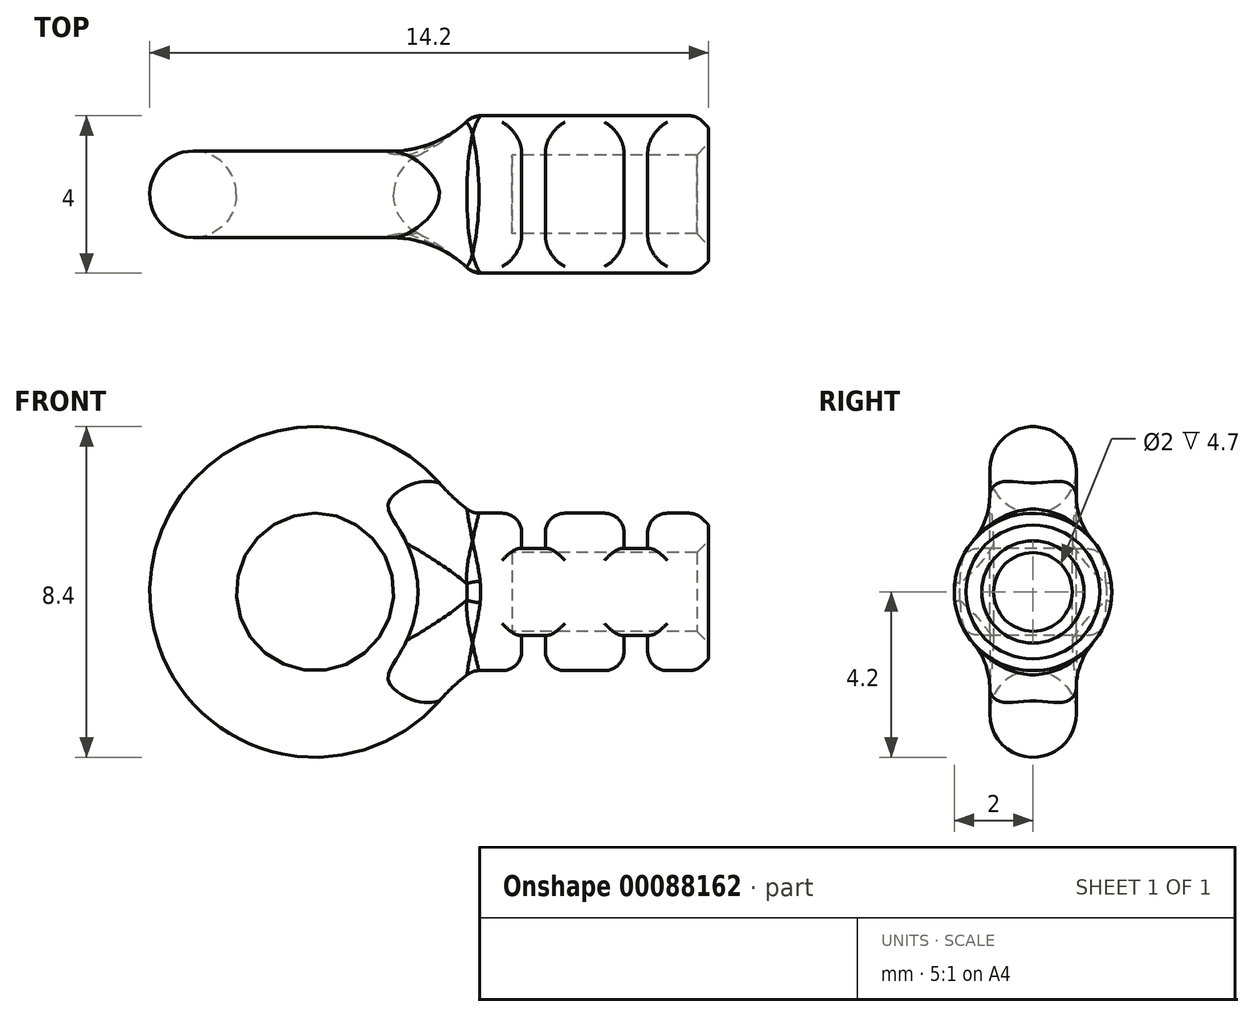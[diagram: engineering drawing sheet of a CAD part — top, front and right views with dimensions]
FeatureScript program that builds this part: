
annotation { "Feature Type Name" : "Feature", "Feature Type Description" : "" }
export const myFeature = defineFeature(function(context is Context, id is Id, definition is map)
    precondition{}
    {
        {
            var Q0;
            Q0=qCreatedBy(makeId("Top.planeOp"),FACE);
            var sketch = newSketch(context, id + "F0", { "sketchPlane" : qUnion([Q0])});
            skLineSegment(sketch, "E0", {"start": v(-5, 0) * mm, "end": v(-5, 1) * mm});
            skLineSegment(sketch, "E1", {"start": v(-5, 1) * mm, "end": v(0, 1) * mm});
            skLineSegment(sketch, "E2", {"start": v(0, 1) * mm, "end": v(0, 2) * mm});
            skLineSegment(sketch, "E3", {"start": v(0, 2) * mm, "end": v(-6, 2) * mm});
            skLineSegment(sketch, "E4", {"start": v(-6, 2) * mm, "end": v(-8, 0) * mm});
            skLineSegment(sketch, "E5", {"start": v(-8, 0) * mm, "end": v(-5, 0) * mm});
            skSolve(sketch);
        }
        {
            var Q0;
            Q0=makeQuery(id+"F0.imprint","IMPRINT",FACE,{"disambiguationData":[TD([[makeQuery(id+"F0.imprint","IMPRINT",EDGE,{"derivedFrom":sQuery(id+"F0.wireOp",EDGE,"E0")}),1.0]])]});
            var Q1;
            Q1=sQuery(id+"F0.wireOp",EDGE,"E5");
            revolve(context, id + "F1", {"entities" : qUnion([Q0]), "axis" : qUnion([Q1]), "revolveType" : RevolveType.FULL});
        }
        {
            var Q0;
            Q0=makeQuery(id+"F1.opRevolve","SWEPT_EDGE",EDGE,{"disambiguationData":[OSD([sQuery(id+"F0.wireOp",EDGE,"E1"),sQuery(id+"F0.wireOp",EDGE,"E2")])]});
            var Q1;
            Q1=makeQuery(id+"F1.opRevolve","SWEPT_EDGE",EDGE,{"disambiguationData":[OSD([sQuery(id+"F0.wireOp",EDGE,"E2"),sQuery(id+"F0.wireOp",EDGE,"E3")])]});
            chamfer(context, id + "F2", {"entities" : qUnion([Q0, Q1]), "width" : .3 * mm, "tangentPropagation" : true});
        }
        {
            var Q0;
            Q0=qCreatedBy(makeId("Front.planeOp"),FACE);
            var sketch = newSketch(context, id + "F3", { "sketchPlane" : qUnion([Q0])});
            skLineSegment(sketch, "E6.bottom", {"start": v(-1.55, 3.34) * mm, "end": v(-2.15, 3.34) * mm});
            skLineSegment(sketch, "E6.top", {"start": v(-1.55, 1.1) * mm, "end": v(-2.15, 1.1) * mm});
            skLineSegment(sketch, "E6.left", {"start": v(-1.55, 3.34) * mm, "end": v(-1.55, 1.1) * mm});
            skLineSegment(sketch, "E6.right", {"start": v(-2.15, 3.34) * mm, "end": v(-2.15, 1.1) * mm});
            skLineSegment(sketch, "E7.bottom", {"start": v(-4.75, 3.7) * mm, "end": v(-4.15, 3.7) * mm});
            skLineSegment(sketch, "E7.top", {"start": v(-4.75, 1.1) * mm, "end": v(-4.15, 1.1) * mm});
            skLineSegment(sketch, "E7.left", {"start": v(-4.75, 3.7) * mm, "end": v(-4.75, 1.1) * mm});
            skLineSegment(sketch, "E7.right", {"start": v(-4.15, 3.7) * mm, "end": v(-4.15, 1.1) * mm});
            skLineSegment(sketch, "E8", {"start": v(-4.15, 1.1) * mm, "end": v(-2.15, 1.1) * mm, "construction": true});
            skLineSegment(sketch, "E9", {"start": v(-3.15, 1.1) * mm, "end": v(-3.15, 0) * mm, "construction": true});
            skLineSegment(sketch, "E10", {"start": v(-6, 0) * mm, "end": v(-0.3, 0) * mm, "construction": true});
            skLineSegment(sketch, "E11.MirrorCS", {"start": v(-1.55, -3.34) * mm, "end": v(-2.15, -3.34) * mm});
            skLineSegment(sketch, "E12.MirrorCS", {"start": v(-1.55, -1.1) * mm, "end": v(-2.15, -1.1) * mm});
            skLineSegment(sketch, "E13.MirrorCS", {"start": v(-4.75, -3.7) * mm, "end": v(-4.15, -3.7) * mm});
            skLineSegment(sketch, "E14.MirrorCS", {"start": v(-1.55, -3.34) * mm, "end": v(-1.55, -1.1) * mm});
            skLineSegment(sketch, "E15.MirrorCS", {"start": v(-4.15, -1.1) * mm, "end": v(-2.15, -1.1) * mm, "construction": true});
            skLineSegment(sketch, "E16.MirrorCS", {"start": v(-3.15, -1.1) * mm, "end": v(-3.15, 0) * mm, "construction": true});
            skLineSegment(sketch, "E17.MirrorCS", {"start": v(-4.75, -1.1) * mm, "end": v(-4.15, -1.1) * mm});
            skLineSegment(sketch, "E18.MirrorCS", {"start": v(-2.15, -3.34) * mm, "end": v(-2.15, -1.1) * mm});
            skLineSegment(sketch, "E19.MirrorCS", {"start": v(-4.75, -3.7) * mm, "end": v(-4.75, -1.1) * mm});
            skLineSegment(sketch, "E20.MirrorCS", {"start": v(-4.15, -3.7) * mm, "end": v(-4.15, -1.1) * mm});
            skSolve(sketch);
        }
        {
            var Q0;
            Q0=makeQuery(id+"F3.imprint","IMPRINT",FACE,{"disambiguationData":[TD([[makeQuery(id+"F3.imprint","IMPRINT",EDGE,{"derivedFrom":sQuery(id+"F3.wireOp",EDGE,"E6.bottom")}),1.0]])]});
            var Q1;
            Q1=makeQuery(id+"F3.imprint","IMPRINT",FACE,{"disambiguationData":[TD([[makeQuery(id+"F3.imprint","IMPRINT",EDGE,{"derivedFrom":sQuery(id+"F3.wireOp",EDGE,"E11.MirrorCS")}),-1.0]])]});
            var Q2;
            Q2=makeQuery(id+"F3.imprint","IMPRINT",FACE,{"disambiguationData":[TD([[makeQuery(id+"F3.imprint","IMPRINT",EDGE,{"derivedFrom":sQuery(id+"F3.wireOp",EDGE,"E13.MirrorCS")}),1.0]])]});
            var Q3;
            Q3=makeQuery(id+"F3.imprint","IMPRINT",FACE,{"disambiguationData":[TD([[makeQuery(id+"F3.imprint","IMPRINT",EDGE,{"derivedFrom":sQuery(id+"F3.wireOp",EDGE,"E7.bottom")}),-1.0]])]});
            extrude(context, id + "F4", {"entities" : qUnion([Q0, Q1, Q2, Q3]), "operationType" : NewBodyOperationType.REMOVE, "endBound" : BoundingType.SYMMETRIC, "oppositeDirection" : true, "depth" : 25 * mm});
        }
        {
            var Q0;
            Q0=qCreatedBy(makeId("Top.planeOp"),FACE);
            var sketch = newSketch(context, id + "F5", { "sketchPlane" : qUnion([Q0])});
            skCircle(sketch, "E21", {"center": v(-6.9, 0) * mm, "radius": 1.1 * mm});
            skLineSegment(sketch, "E22", {"start": v(-8, 0) * mm, "end": v(-10, 0) * mm, "construction": true});
            skLineSegment(sketch, "E23", {"start": v(-10, 0) * mm, "end": v(-10, -0.84) * mm, "construction": true});
            skSolve(sketch);
        }
        {
            var Q0;
            Q0 = qSketchRegion(id + "F5", true);
            var Q1;
            Q1=sQuery(id+"F5.wireOp",EDGE,"E23");
            revolve(context, id + "F6", {"operationType" : NewBodyOperationType.ADD, "entities" : qUnion([Q0]), "axis" : qUnion([Q1]), "revolveType" : RevolveType.FULL});
        }
        {
            var Q0;
            Q0=makeQuery(id+"F6.boolean.opBoolean","INTERSECT",EDGE,{"derivedFrom":[makeQuery(id+"F1.opRevolve","SWEPT_FACE",FACE,{"disambiguationData":[OSD([sQuery(id+"F0.wireOp",EDGE,"E4")])]}),makeQuery(id+"F6.opRevolve","SWEPT_FACE",FACE,{"disambiguationData":[OSD([sQuery(id+"F5.wireOp",EDGE,"E21")])]})]});
            fillet(context, id + "F7", {"entities" : qUnion([Q0]), "radius" : 5 * mm, "tangentPropagation" : true, "allowEdgeOverflow" : false});
        }
        {
            var Q0;
            Q0=makeQuery(id+"F7.opFillet","BLEND_EDGE",EDGE,{"disambiguationData":[OD(0.0)],"blendedFrom":[makeQuery(id+"F6.boolean.opBoolean","INTERSECT",EDGE,{"derivedFrom":[makeQuery(id+"F1.opRevolve","SWEPT_FACE",FACE,{"disambiguationData":[OSD([sQuery(id+"F0.wireOp",EDGE,"E4")])]}),makeQuery(id+"F6.opRevolve","SWEPT_FACE",FACE,{"disambiguationData":[OSD([sQuery(id+"F5.wireOp",EDGE,"E21")])]})]}),makeQuery(id+"F1.opRevolve","SWEPT_FACE",FACE,{"disambiguationData":[OSD([sQuery(id+"F0.wireOp",EDGE,"E3")])]})],"blendedInto":[makeQuery(id+"F1.opRevolve","SWEPT_FACE",FACE,{"disambiguationData":[OSD([sQuery(id+"F0.wireOp",EDGE,"E3")])]})]});
            var Q1;
            Q1=makeQuery(id+"F7.opFillet","BLEND_EDGE",EDGE,{"disambiguationData":[OD(1.0)],"blendedFrom":[makeQuery(id+"F6.boolean.opBoolean","INTERSECT",EDGE,{"derivedFrom":[makeQuery(id+"F1.opRevolve","SWEPT_FACE",FACE,{"disambiguationData":[OSD([sQuery(id+"F0.wireOp",EDGE,"E4")])]}),makeQuery(id+"F6.opRevolve","SWEPT_FACE",FACE,{"disambiguationData":[OSD([sQuery(id+"F5.wireOp",EDGE,"E21")])]})]}),makeQuery(id+"F1.opRevolve","SWEPT_FACE",FACE,{"disambiguationData":[OSD([sQuery(id+"F0.wireOp",EDGE,"E3")])]})],"blendedInto":[makeQuery(id+"F1.opRevolve","SWEPT_FACE",FACE,{"disambiguationData":[OSD([sQuery(id+"F0.wireOp",EDGE,"E3")])]})]});
            var Q2;
            Q2=makeQuery(id+"F1.opRevolve","SWEPT_EDGE",EDGE,{"disambiguationData":[OSD([sQuery(id+"F0.wireOp",EDGE,"E3"),sQuery(id+"F0.wireOp",EDGE,"E4")])]});
            var Q3;
            Q3=makeQuery(id+"F1.opRevolve","SWEPT_FACE",FACE,{"disambiguationData":[OSD([sQuery(id+"F0.wireOp",EDGE,"E3")])]});
            fillet(context, id + "F8", {"entities" : qUnion([Q0, Q1, Q2, Q3]), "radius" : .5 * mm, "tangentPropagation" : true, "allowEdgeOverflow" : false});
        }
    });
